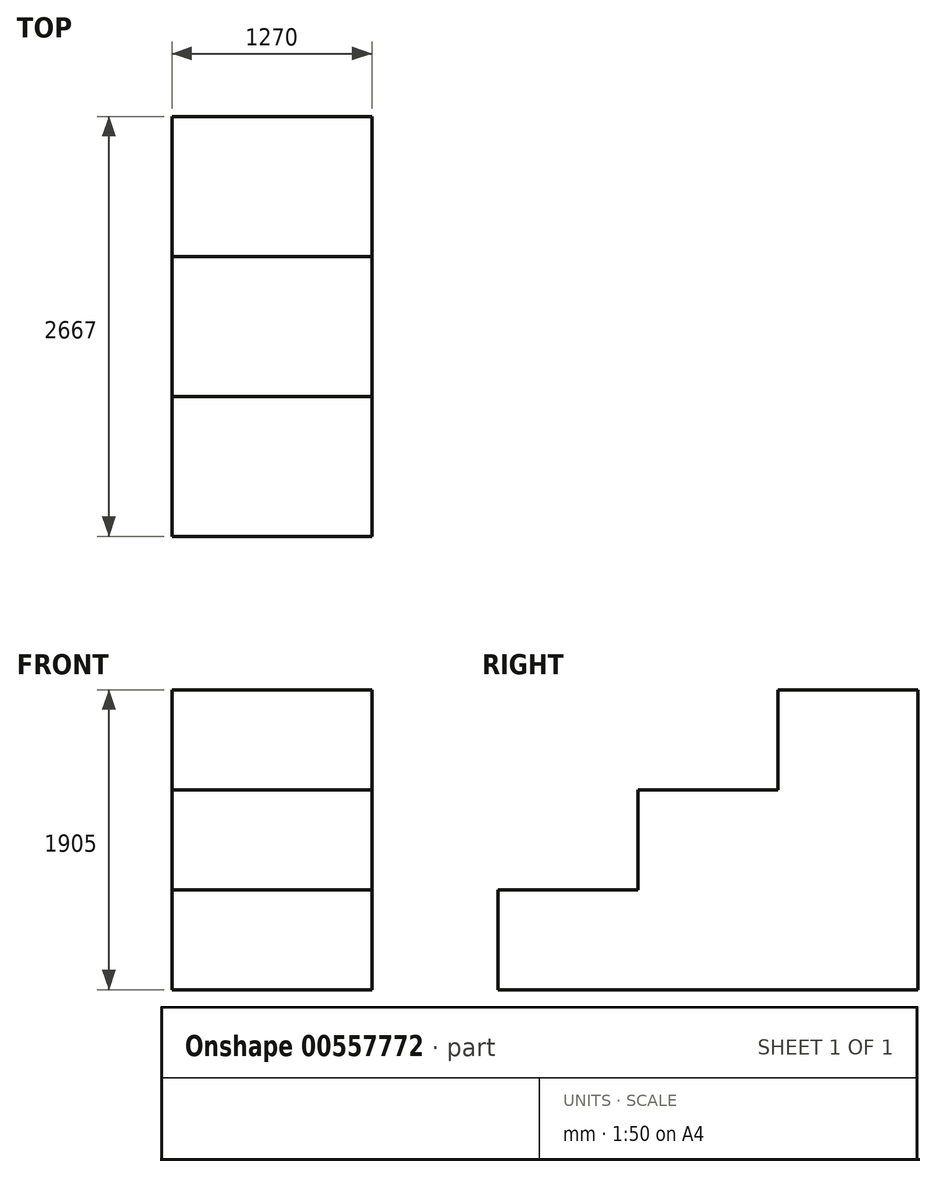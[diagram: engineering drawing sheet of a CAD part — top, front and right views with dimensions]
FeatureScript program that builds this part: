
annotation { "Feature Type Name" : "Feature", "Feature Type Description" : "" }
export const myFeature = defineFeature(function(context is Context, id is Id, definition is map)
    precondition{}
    {
        {
            var Q0;
            Q0=qCreatedBy(makeId("Front.planeOp"),FACE);
            var sketch = newSketch(context, id + "F0", { "sketchPlane" : qUnion([Q0])});
            skLineSegment(sketch, "E0", {"start": v(-52.32, 1865.85) * mm, "end": v(-52.32, -39.15) * mm});
            skLineSegment(sketch, "E1", {"start": v(-52.32, -39.15) * mm, "end": v(1217.68, -39.15) * mm});
            skLineSegment(sketch, "E2", {"start": v(1217.68, -39.15) * mm, "end": v(1217.68, 1865.85) * mm});
            skLineSegment(sketch, "E3", {"start": v(1217.68, 1865.85) * mm, "end": v(-52.32, 1865.85) * mm});
            skSolve(sketch);
        }
        {
            var Q0;
            Q0=makeQuery(id+"F0.imprint","IMPRINT",FACE,{"disambiguationData":[TD([[makeQuery(id+"F0.imprint","IMPRINT",EDGE,{"derivedFrom":sQuery(id+"F0.wireOp",EDGE,"E0")}),1.0]])]});
            extrude(context, id + "F1", {"entities" : qUnion([Q0]), "oppositeDirection" : true, "depth" : 2667 * mm, "offsetDistance" : 25.4 * mm});
        }
        {
            var Q0;
            Q0=makeQuery(id+"F1.opExtrude","SWEPT_FACE",FACE,{"disambiguationData":[OSD([sQuery(id+"F0.wireOp",EDGE,"E3")])]});
            var sketch = newSketch(context, id + "F2", { "sketchPlane" : qUnion([Q0])});
            skLineSegment(sketch, "E4", {"start": v(-52.32, 0) * mm, "end": v(-52.32, 889) * mm});
            skLineSegment(sketch, "E5", {"start": v(-52.32, 889) * mm, "end": v(1217.68, 889) * mm});
            skSolve(sketch);
        }
        {
            var Q0;
            Q0=makeQuery(id+"F2.imprint","IMPRINT",FACE,{"disambiguationData":[TD([[makeQuery(id+"F2.imprint","IMPRINT",EDGE,{"derivedFrom":sQuery(id+"F2.wireOp",EDGE,"E4")}),1.0]])]});
            extrude(context, id + "F3", {"entities" : qUnion([Q0]), "operationType" : NewBodyOperationType.REMOVE, "oppositeDirection" : true, "depth" : 1270 * mm, "offsetDistance" : 25.4 * mm});
        }
        {
            var Q0;
            Q0=makeQuery(id+"F1.opExtrude","SWEPT_FACE",FACE,{"disambiguationData":[OSD([sQuery(id+"F0.wireOp",EDGE,"E3")])]});
            var sketch = newSketch(context, id + "F4", { "sketchPlane" : qUnion([Q0])});
            skLineSegment(sketch, "E6", {"start": v(-52.32, 889) * mm, "end": v(-52.32, 1778) * mm});
            skLineSegment(sketch, "E7", {"start": v(-52.32, 1778) * mm, "end": v(1217.68, 1778) * mm});
            skSolve(sketch);
        }
        {
            var Q0;
            Q0=makeQuery(id+"F4.imprint","IMPRINT",FACE,{"disambiguationData":[TD([[makeQuery(id+"F4.imprint","IMPRINT",EDGE,{"derivedFrom":sQuery(id+"F4.wireOp",EDGE,"E6")}),1.0]])]});
            extrude(context, id + "F5", {"entities" : qUnion([Q0]), "operationType" : NewBodyOperationType.REMOVE, "oppositeDirection" : true, "depth" : 635 * mm, "offsetDistance" : 25.4 * mm});
        }
    });
